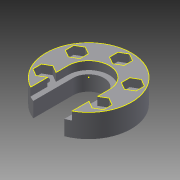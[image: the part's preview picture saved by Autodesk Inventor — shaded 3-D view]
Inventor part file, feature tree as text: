
AUTODESK INVENTOR PART (.ipt)
format: ipt  version: 2013 (Build 170138000, 138)  size: 191,488 bytes
history: native  units: mm
features: sketch x6, extrude x4
ambient origin geometry x8: Origin, YZ Plane, XZ Plane, XY Plane, X Axis, Y Axis, Z Axis, Center Point
bodies: Solid1 (feature_tree), Body (feature_tree)
feature tree (10):
  extrude  "Main Cutout"  Depth=9.0mm TaperAngle=0.0deg
  extrude  "Bottom Cutout"  Depth=9.0mm TaperAngle=0.0deg
  extrude  "M3 Holes"  Depth=3.2mm TaperAngle=0.0deg
  extrude  "M3 Nut Traps"  Depth=3.2mm
  sketch  "Sketch9"  dims[d24=7.0mm d25=0.0mm d26=25.0mm d27=3.0mm d28=60.0mm d30=360.0deg d32=5.65mm d33=5.65mm d34=5.65mm d35=5.66mm d36=5.66mm d37=3.2mm d38=0.0mm]
  sketch  "Sketch1"  dims[d0=33.0mm d1=9.0mm d2=0.0mm]
  sketch  "Sketch2"  dims[d3=12.0mm d4=9.0mm d5=0.0mm]
  sketch  "Sketch4"  dims[d7=16.0mm d8=3.2mm d9=0.0mm]
  sketch  "Sketch7"  dims[d18=25.0mm d19=3.2mm]
  sketch  "Sketch8"  dims[d20=60.0mm d22=360.0deg]
